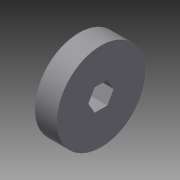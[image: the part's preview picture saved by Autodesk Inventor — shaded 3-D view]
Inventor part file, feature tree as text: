
AUTODESK INVENTOR PART (.ipt)
format: ipt  version: 2015 SP1 (Build 190203100, 203)  size: 90,624 bytes
history: native  units: in
note: dims shown in document units (in); Inventor stores cm internally (conversion verified against a paired STEP export)
features: extrude x2, sketch x2
ambient origin geometry x8: Origin, YZ Plane, XZ Plane, XY Plane, X Axis, Y Axis, Z Axis, Center Point
bodies: Solid1 (feature_tree)
feature tree (4):
  extrude  "Extrusion1"  Depth=0.5in TaperAngle=0.0deg
  extrude  "Extrusion2"  Depth=0.5in
  sketch  "Sketch1"  dims[d0=2.0in d1=0.5in d2=0.0in]
  sketch  "Sketch2"  dims[d3=0.5in d4=0.5in d5=0.5in d6=0.25in d7=0.25in d8=0.25in d9=120.0deg d10=120.0deg d11=0.5in d12=0.0in]
